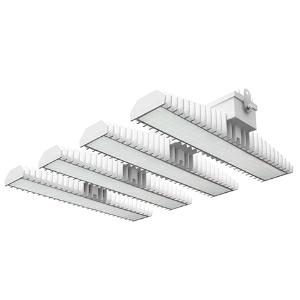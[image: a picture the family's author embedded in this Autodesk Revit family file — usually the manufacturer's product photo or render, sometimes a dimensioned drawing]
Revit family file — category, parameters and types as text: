
# Revit family: 3f_filippi_-_3f_lem_concentrato_3f_filippi_-_58908_a0812_-_3f_lem_4_led_200_dali_cr_conc___vs_7993
name_source: partatom
category: Lighting Fixtures
units: mm (PartAtom-declared; Revit-internal decimal feet)

## family parameters
Cut with Voids When Loaded = No
Host = Face
Light Source = No
Part Type = Normal
Room Calculation Point = No
Round Connector Dimension = Use Diameter
Shared = No

## types (1)
- 3F Filippi - 3F LEM Concentrato (1 x LED, 26428 lm, 218 W, 4000 K)
    Apparent Load = 218 VA
    Approval mark = CE
    CIE Flux Codes = 78 93 98 100 100
    Color Rendering = 80
    Color Temperature = 4000 K
    Control Gear = Electronic transformer
    Default Elevation = 1800 mm
    Description = Industrial luminaire with high light output and high luminous efficiency designed with the most innovative technologies for environments with temperature up to 55°C.

ILLUMINOTECHNICAL
Luminous efficiency 100% (DLOR 98%, ULOR 2%).
Initial luminous flux of the luminaire 26428 lm.
Direct symmetric narrow distribution: the illuminated area has a elliptical shape.
Installation Interdistance Transv.D = 0.60 x hu - Long.D = 0.91 x hu.
Tabular UGR (CIE 117 - 4H-8H; S=0.25H; 70/50/20): RUG 20.2 - 21.8.
Beam angle: 38° - 61°.
Luminous efficacy 121 lm/W.
Lifetime (L93/B10): 30000 h. (tq+25°C)
Lifetime (L90/B10): 50000 h. (tq+25°C)
Lifetime (L85/B10): 80000 h. (tq+25°C)
Lifetime (L80/B10): 100000 h. (tq+25°C)
Lifetime (L85/B10): 50000 h. (tq+55°C)
Sudden decreased luminous flux after 50000 hours: 0% (C0).
Photobiological safety in compliance with IEC/TR 62778: RG0 risk exempt, (IEC 62471).
In compliance with IEC/EN 62722-2-1 - IEC/EN 62717 standards.

SOURCE
4 Mid-Power linear LED modules 50W/840.
Energy efficiency class (UE 2019/2020 - UE 2019/2015): C.
CIE 13.3 Colour rendering index: CRI >80 (R9 <50%).
IES TM-30 Fidelity Index: Rf = 84 Rg = 95.
CCT nominal colour temperature 4000 K.
Colour initial tolerance (MacAdam): SDCM 3.

MECHANICAL
Passive modular heatsinks in die-casted aluminium, painted in white colour.
To optimize the thermal management of the LED module, the heatsinks are oversized and provided with self-cleaning of cooling fins.
Wiring body in aluminium and galvanised steel anchored solidly to the sinks and thermally separated.
3F Lens lenses with high luminous efficiency, transparent methacrylate (PMMA), fixed to the LED modules.
Fixing brackets in stainless steel.
Luminaire with limited surface temperature. - D - (EN 60598-2-24)
Dimensions: 757x542 mm, height 133 mm. Weight 18.64 kg.
IP65 protection degree.
Mechanical strength to impacts IK06 (1 joule).
Glow-wire test resistance 650°C.

ELECTRICAL
Halogen Free DALI-2 DATI (Parts 251, 252, 253), PUSH-DIM, electronic wiring 230V-50/60Hz, power factor 0.97 at full load, THD <25%, constant output current, class I, 2 driver, 2 DALI addresses.
Power of the luminaire 218 W.
ENEC - CE.
Flicker: <4%.
Luminaire compliant with EN 60598-2-22 for power supply from a centralised emergency system CPSS (Central Power Supply System), not incorporated in the luminaire - high risk areas excluded. The default power and flux are 100% in AC and 15% in DC.
Ambient temperature from -30°C to +55°C.
Temperature class T6 max 85°C.
Quick connection via M25 5P connector with 9-13 mm tightening range.
Power unit positioned on a separate compartment by the LED module to ensure optimum temperatures of cabling components, to be inspectable and maintainable.
Relative humidity UR: <85%.

INSTALLATION
Ceiling / Suspended / Wall.
All accessories dedicated to this product are available on the Catalog and on our website www.3F-Filippi.com.

ACCESSORIES
A0812 - Anti-glare microprismatic VS moulded glass, tempered, not flammable, with sealing gasket.
One required for each light module. The pack contains 10 pieces.

APPLICATIONS
In commercial environments, exhibition and industrial areas, stores, open areas or with shelves.
Applications with high ambient temperature up to 55°C.
Environments in which it is necessary a total protection against falling fragments (eg environments with foodstuffs or machines with moving parts or with extreme temperature changes), use luminaires with polycarbonate lenses.

LIGHT MANAGEMENT
Recommended minimum setting: 10%.
The luminaire, equipped with (DALI-2 DATI) driver, can be controlled manually with 3F Easy Dim technology or automatically/manually with wired or wireless DALI/D2D control systems.
The D2D driver guarantees interoperability with other devices with the same certification by making the following information available:
Device Data (Part 251), Energy Report (Part 252), Diagnosis & Maintenance (Part 253).
In electrical systems without a regulation system (manual or automatic) and DALI bus, a suitable jumper must be made on the DA-DA terminals of the appliance.

WARNING
Fixture not suitable for cold stores with an ambient temperature <0°C and/or relative humidity >85%.
Luminaire designed for disposal/recycling at end-of-life.
Replaceable (LED only) light source by a professional. Replaceable control gear by a professional.
    Height = 133 mm  [stored 0.436352 ft]
    Lamp = 1 x LED
    Lamp Light Flux = 26428 lm
    Lamp Power = 218 W
    Lamp count = 1
    Length = 757 mm
    Lifetime = 50000 h
    Luminous efficacy = 121 lm/W
    Manufacturer = 3F Filippi
    ModVariant = No
    Model = 3F Filippi - 58908+A0812 - 3F LEM 4 LED 200 DALI CR CONC + VS
    Mounting Place = Ceiling
    Mounting Type = Pendant
    Number of Poles = 1
    OnlyDefault = Yes
    Power Factor = 1
    Product Name = 3F Filippi - 3F LEM Concentrato
    Product group = pendant luminaire
    ProductGroupID = 9
    Protection Class = Protection class I
    Protection Degree = IP 65
    RLX_Detail_Level = 1
    RLX_Emergency_Light_Flux = 0 lm
    RLX_Emergency_Type = 0
    RLX_Emergency_Type_DB = No
    RlxData = <blob elided: 122869 chars, md5=9c48dee6>
    Socket = socket
    Standby Power = 0 W
    System Light Flux = 26428 lm
    System Power = 218 W
    Type Comments = Product without accessories
    Type Image = 3f_filippi_-_lem_4__a0812.jpg
    URL = http://relux.com
    VarID = ---
    Voltage = 0 V
    Weight = 0.00 kg
    Width = 542 mm

note: [stored X ft] marks values corroborated as IEEE doubles in the binary element streams (Revit-internal decimal feet)

## geometry (parser evidence)
native form markers: Blend x4, Sweep x12
no freeform markers — native parametric forms only
